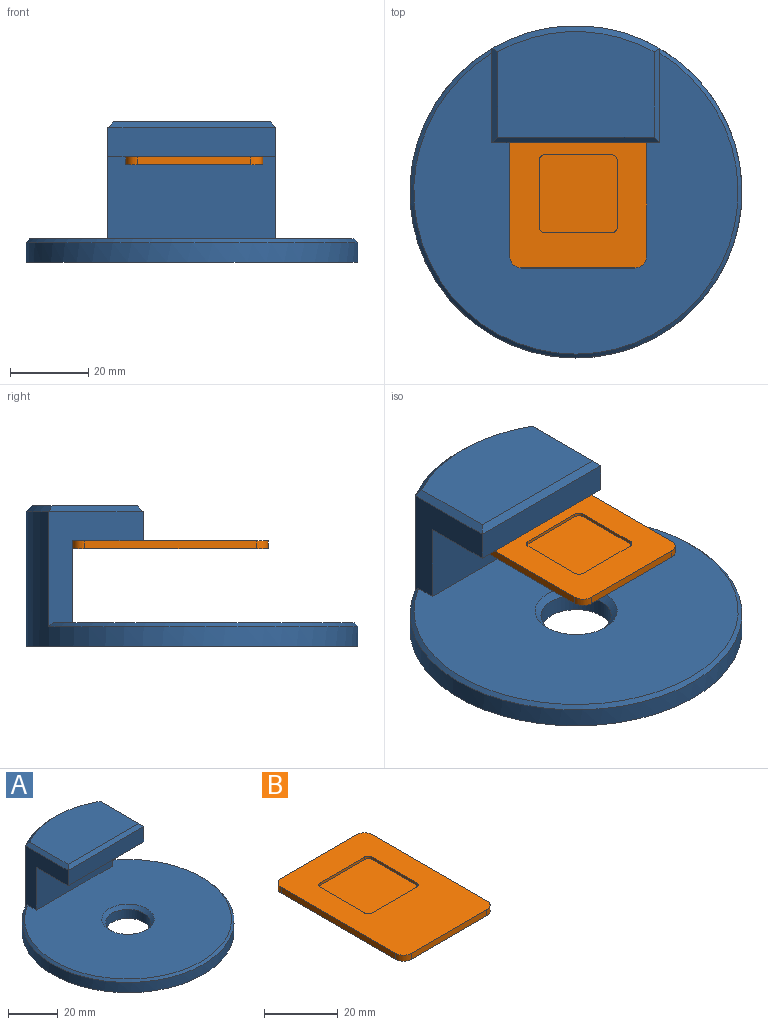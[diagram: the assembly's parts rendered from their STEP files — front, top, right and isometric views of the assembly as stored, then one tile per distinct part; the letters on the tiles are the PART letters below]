
ASSEMBLY  parts=2 mates=2
PART A: 16 faces, bbox 85x85x36 mm
  f0: plane 29.51x24.17mm, normal (1,0,0), area 311.2mm2, adj f1,f3,f6,f8,f9,f10,f15
  f1: plane 83x77mm, normal (0,0,1), area 4674.6mm2, adj f0,f5,f9,f14,f15
  f2: cylinder r=9mm len=18mm, axis (0,0,-1), area 254.5mm2, adj f4,f14
  f3: cylinder r=42.5mm len=85mm, axis (0,0,-1), area 2665.2mm2, adj f0,f4,f5,f11,f15
  f4: plane 85x85mm, normal (0,0,-1), area 5420mm2, adj f2,f3
  f5: plane 29.51x24.17mm, normal (-1,0,0), area 311.2mm2, adj f1,f3,f6,f8,f9,f13,f15
  f6: plane 43x7.5mm, normal (0,-1,0), area 322.5mm2, adj f0,f5,f8,f12
  f7: plane 40x27mm, normal (0,0,1), area 1012.4mm2, adj f10,f11,f12,f13
  f8: plane 43x18mm, normal (0,0,-1), area 774mm2, adj f0,f5,f6,f9
  f9: plane 43x21mm, normal (0,-1,0), area 903mm2, adj f0,f1,f5,f8
  f10: plane 24.17x1.51mm, normal (0.71,0,0.71), area 48.7mm2, adj f0,f7,f11,f12
  f11: cone r=41mm half-angle=45deg, axis (0,0,-1), area 92.1mm2, adj f3,f7,f10,f13
  f12: plane 43x1.5mm, normal (0,-0.71,0.71), area 88mm2, adj f6,f7,f10,f13
  f13: plane 24.17x1.51mm, normal (-0.71,0,0.71), area 48.7mm2, adj f5,f7,f11,f12
  f14: cone r=9mm half-angle=45deg, axis (0,0,1), area 130mm2, adj f1,f2
  f15: cone r=41.5mm half-angle=45deg, axis (0,0,-1), area 309.4mm2, adj f0,f1,f3,f5
PART B: 19 faces, bbox 35x50x2 mm
  f0: plane 29x2mm, normal (0,-1,0), area 58mm2, adj f1,f7,f8,f9
  f1: cylinder r=3mm len=3mm, axis (0,0,-1), area 9.4mm2, adj f0,f2,f8,f9
  f2: plane 44x2mm, normal (1,0,0), area 88mm2, adj f1,f3,f8,f9
  f3: cylinder r=3mm len=3mm, axis (0,0,-1), area 9.4mm2, adj f2,f4,f8,f9
  f4: plane 29x2mm, normal (0,1,0), area 58mm2, adj f3,f5,f8,f9
  f5: cylinder r=3mm len=3mm, axis (0,0,-1), area 9.4mm2, adj f4,f6,f8,f9
  f6: plane 44x2mm, normal (-1,0,0), area 88mm2, adj f5,f7,f8,f9
  f7: cylinder r=3mm len=3mm, axis (0,0,-1), area 9.4mm2, adj f0,f6,f8,f9
  f8: plane 50x35mm, normal (0,0,1), area 1344.2mm2, adj f0,f1,f2,f3,f4,f5,f6,f7
  f9: plane 50x35mm, normal (0,0,-1), area 1742.3mm2, adj f0,f1,f2,f3,f4,f5,f6,f7
  f10: cylinder r=1.5mm len=1.5mm, axis (0,0,1), area 1.9mm2, adj f8,f11,f17,f18
  f11: plane 17x0.8mm, normal (0,-1,0), area 13.6mm2, adj f8,f10,f12,f18
  f12: cylinder r=1.5mm len=1.5mm, axis (0,0,1), area 1.9mm2, adj f8,f11,f13,f18
  f13: plane 17x0.8mm, normal (1,0,0), area 13.6mm2, adj f8,f12,f14,f18
  f14: cylinder r=1.5mm len=1.5mm, axis (0,0,1), area 1.9mm2, adj f8,f13,f15,f18
  f15: plane 17x0.8mm, normal (0,1,0), area 13.6mm2, adj f8,f14,f16,f18
  f16: cylinder r=1.5mm len=1.5mm, axis (0,0,1), area 1.9mm2, adj f8,f15,f17,f18
  f17: plane 17x0.8mm, normal (-1,0,0), area 13.6mm2, adj f8,f10,f16,f18
  f18: plane 20x20mm, normal (0,0,1), area 398.1mm2, adj f10,f11,f12,f13,f14,f15,f16,f17
PLACE A t=(0.61,0.5,-17.78)mm fixed
PLACE B rot(axis=(0,0,-1),180deg) t=(1.21,6,7.22)mm
MATE planar B.f0 <-> A.f9  axis (0,1,0) through (1.21,31,9.22)mm
MATE planar B.f8 <-> A.f8  axis (0,0,1) through (1.21,10,9.22)mm
